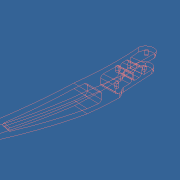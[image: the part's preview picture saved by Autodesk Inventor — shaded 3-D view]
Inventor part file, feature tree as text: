
AUTODESK INVENTOR PART (.ipt)
format: ipt  version: unknown  size: 261,120 bytes
history: native  units: mm
features: extrude x2, sketch x2
ambient origin geometry x8: Origin, YZ Plane, XZ Plane, XY Plane, X Axis, Y Axis, Z Axis, Center Point
feature tree (4):
  extrude  "Выдавливание1"  Depth=1.2mm
  extrude  "Выдавливание2"  Depth=7.5mm TaperAngle=0.0deg
  sketch  "Эскиз1"
  sketch  "Эскиз2"
